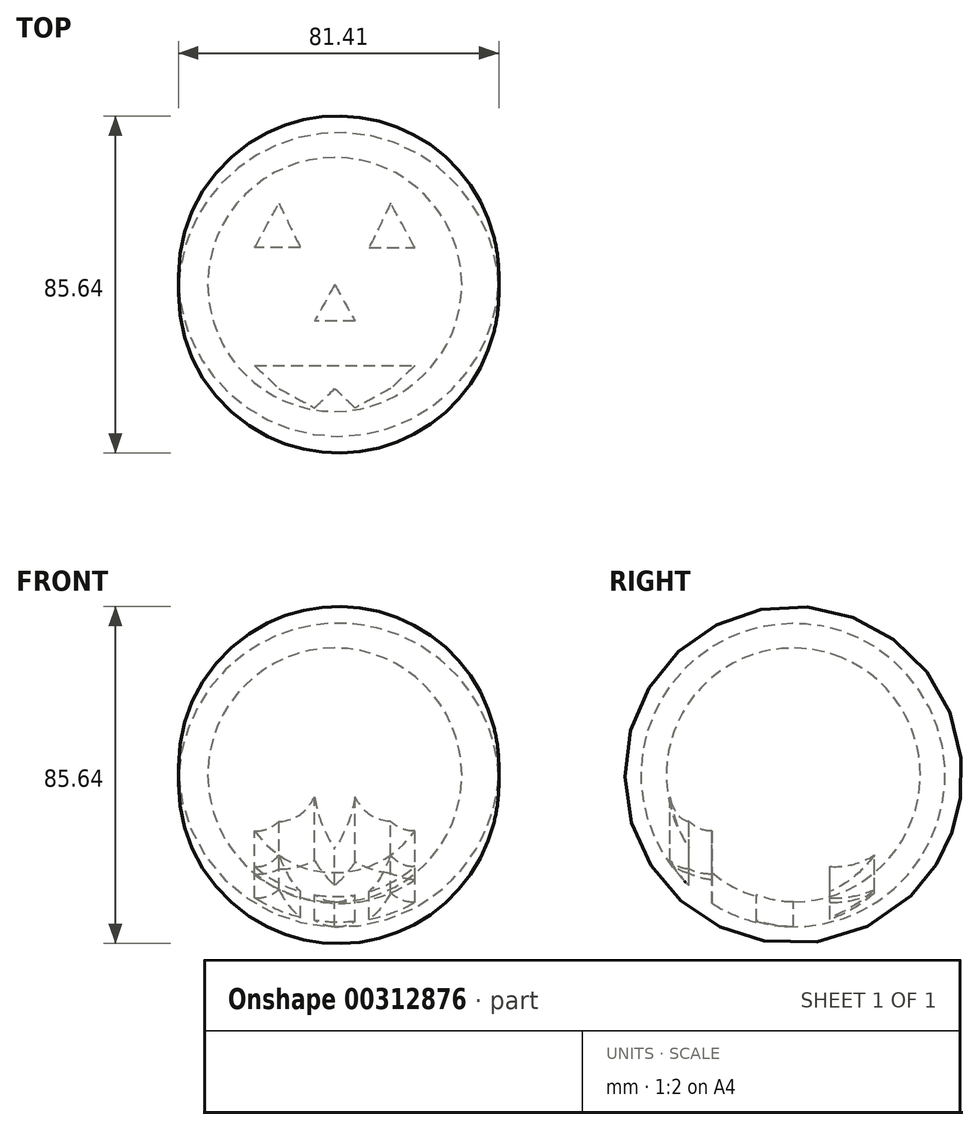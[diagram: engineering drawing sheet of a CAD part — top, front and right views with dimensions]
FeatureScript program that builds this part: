
annotation { "Feature Type Name" : "Feature", "Feature Type Description" : "" }
export const myFeature = defineFeature(function(context is Context, id is Id, definition is map)
    precondition{}
    {
        {
            var Q0;
            Q0=qCreatedBy(makeId("Top.planeOp"),FACE);
            var sketch = newSketch(context, id + "F0", { "sketchPlane" : qUnion([Q0])});
            skArc(sketch, "E0", {"start": v(41.62, 0) * mm, "mid": v(0.97, 38.59) * mm, "end": v(-39.68, 0) * mm});
            skLineSegment(sketch, "E1", {"start": v(-39.68, 0) * mm, "end": v(-32.26, 0) * mm});
            skLineSegment(sketch, "E2.bottom", {"start": v(0, 38.58) * mm, "end": v(-5.16, 38.58) * mm});
            skArc(sketch, "E3", {"start": v(32.26, 0) * mm, "mid": v(0, 32.26) * mm, "end": v(-32.26, 0) * mm});
            skLineSegment(sketch, "E4.trimOffspring", {"start": v(32.26, 0) * mm, "end": v(41.62, 0) * mm});
            skSolve(sketch);
        }
        {
            var Q0;
            Q0=makeQuery(id+"F0.imprint","IMPRINT",FACE,{"disambiguationData":[TD([[makeQuery(id+"F0.imprint","IMPRINT",EDGE,{"derivedFrom":sQuery(id+"F0.wireOp",EDGE,"E0")}),1.0]])]});
            var Q1;
            Q1=sQuery(id+"F0.wireOp",EDGE,"E1");
            revolve(context, id + "F1", {"entities" : qUnion([Q0]), "axis" : qUnion([Q1]), "revolveType" : RevolveType.FULL});
        }
        {
            var Q0;
            Q0=qCreatedBy(makeId("Top.planeOp"),FACE);
            var sketch = newSketch(context, id + "F2", { "sketchPlane" : qUnion([Q0])});
            skLineSegment(sketch, "E5", {"start": v(20.33, 9.36) * mm, "end": v(14.2, 20.65) * mm});
            skLineSegment(sketch, "E6", {"start": v(14.2, 20.65) * mm, "end": v(8.71, 9.36) * mm});
            skLineSegment(sketch, "E7", {"start": v(8.71, 9.36) * mm, "end": v(20.33, 9.36) * mm});
            skLineSegment(sketch, "E8", {"start": v(0, 0) * mm, "end": v(5.16, -9.36) * mm});
            skLineSegment(sketch, "E9", {"start": v(5.16, -9.36) * mm, "end": v(0, -9.36) * mm});
            skLineSegment(sketch, "E10", {"start": v(0, -20.65) * mm, "end": v(20.33, -20.65) * mm});
            skLineSegment(sketch, "E11", {"start": v(20.33, -20.65) * mm, "end": v(14.2, -26.45) * mm});
            skLineSegment(sketch, "E12", {"start": v(14.2, -26.45) * mm, "end": v(5.16, -31.36) * mm});
            skLineSegment(sketch, "E13", {"start": v(5.16, -31.36) * mm, "end": v(0, -26.45) * mm});
            skLineSegment(sketch, "E14", {"start": v(0, -9.36) * mm, "end": v(0, -20.65) * mm});
            skLineSegment(sketch, "E15.MirrorCS", {"start": v(-20.33, 9.36) * mm, "end": v(-14.2, 20.65) * mm});
            skLineSegment(sketch, "E16.MirrorCS", {"start": v(-14.2, 20.65) * mm, "end": v(-8.71, 9.36) * mm});
            skLineSegment(sketch, "E17.MirrorCS", {"start": v(-8.71, 9.36) * mm, "end": v(-20.33, 9.36) * mm});
            skLineSegment(sketch, "E18.MirrorCS", {"start": v(0, 0) * mm, "end": v(-5.16, -9.36) * mm});
            skLineSegment(sketch, "E19.MirrorCS", {"start": v(0, -20.65) * mm, "end": v(-20.33, -20.65) * mm});
            skLineSegment(sketch, "E20.MirrorCS", {"start": v(-20.33, -20.65) * mm, "end": v(-14.2, -26.45) * mm});
            skLineSegment(sketch, "E21.MirrorCS", {"start": v(-14.2, -26.45) * mm, "end": v(-5.16, -31.36) * mm});
            skLineSegment(sketch, "E22.MirrorCS", {"start": v(-5.16, -31.36) * mm, "end": v(0, -26.45) * mm});
            skLineSegment(sketch, "E23", {"start": v(0, -9.36) * mm, "end": v(-5.16, -9.36) * mm});
            skSolve(sketch);
        }
        {
            var Q0;
            Q0 = qSketchRegion(id + "F2", true);
            extrude(context, id + "F3", {"entities" : qUnion([Q0]), "operationType" : NewBodyOperationType.REMOVE, "oppositeDirection" : true, "depth" : 254 * mm});
        }
    });
